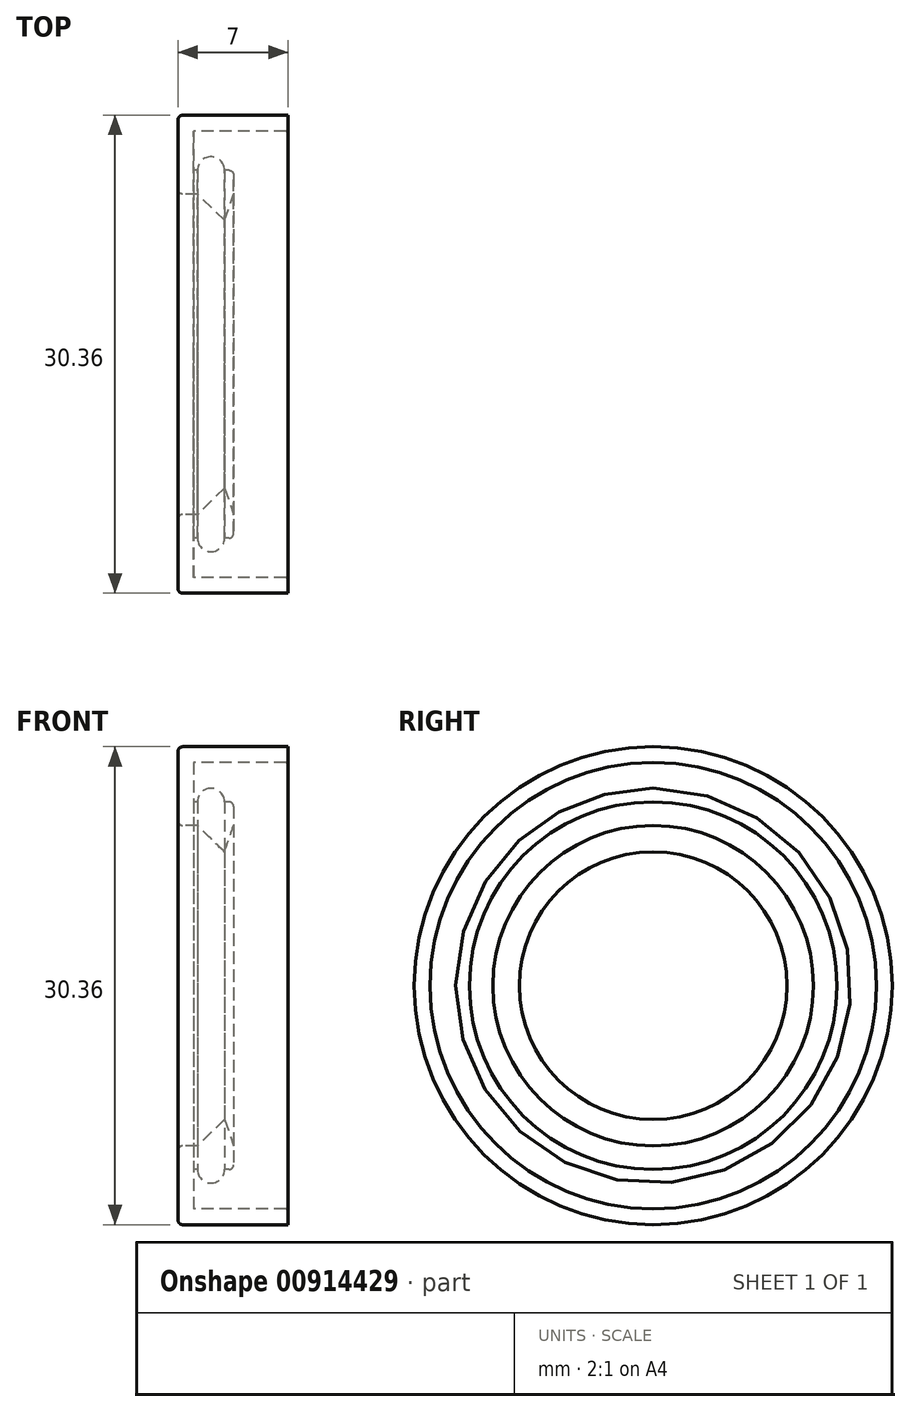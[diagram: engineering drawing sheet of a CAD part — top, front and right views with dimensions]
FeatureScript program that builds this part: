
annotation { "Feature Type Name" : "Feature", "Feature Type Description" : "" }
export const myFeature = defineFeature(function(context is Context, id is Id, definition is map)
    precondition{}
    {
        {
            var Q0;
            Q0=qCreatedBy(makeId("Front.planeOp"),FACE);
            var sketch = newSketch(context, id + "F0", { "sketchPlane" : qUnion([Q0])});
            skLineSegment(sketch, "E0", {"start": v(0, 15.18) * mm, "end": v(0, 0) * mm, "construction": true});
            skLineSegment(sketch, "E1", {"start": v(0, 0) * mm, "end": v(16, 0) * mm, "construction": true});
            skLineSegment(sketch, "E2", {"start": v(3.47, 15.18) * mm, "end": v(-3.23, 15.18) * mm});
            skLineSegment(sketch, "E3", {"start": v(-3.53, 14.88) * mm, "end": v(-3.53, 10.48) * mm});
            skLineSegment(sketch, "E4", {"start": v(-3.23, 10.18) * mm, "end": v(-2.3, 10.18) * mm});
            skLineSegment(sketch, "E5", {"start": v(-2.3, 10.18) * mm, "end": v(-0.58, 8.5) * mm});
            skLineSegment(sketch, "E6", {"start": v(-0.58, 8.5) * mm, "end": v(0, 10.18) * mm});
            skLineSegment(sketch, "E7", {"start": v(0, 10.18) * mm, "end": v(0, 11.38) * mm});
            skLineSegment(sketch, "E8", {"start": v(-0.3, 11.68) * mm, "end": v(-0.58, 11.68) * mm});
            skArc(sketch, "E9", {"start": v(-0.58, 11.68) * mm, "mid": v(-1.44, 12.54) * mm, "end": v(-2.3, 11.68) * mm});
            skLineSegment(sketch, "E10", {"start": v(-2.3, 11.68) * mm, "end": v(-2.53, 11.68) * mm});
            skLineSegment(sketch, "E11", {"start": v(-2.53, 11.68) * mm, "end": v(-2.53, 14.18) * mm});
            skLineSegment(sketch, "E12", {"start": v(-2.53, 14.18) * mm, "end": v(3.32, 14.18) * mm});
            skLineSegment(sketch, "E13", {"start": v(3.47, 14.32) * mm, "end": v(3.47, 15.18) * mm});
            skPoint(sketch, "E14.visualSharp", {"position": v(3.47, 14.18) * mm});
            skArc(sketch, "E14.filletArc", {"start": v(3.32, 14.18) * mm, "mid": v(3.43, 14.22) * mm, "end": v(3.47, 14.32) * mm});
            skPoint(sketch, "E15.visualSharp", {"position": v(-3.53, 15.18) * mm});
            skArc(sketch, "E15.filletArc", {"start": v(-3.23, 15.18) * mm, "mid": v(-3.44, 15.1) * mm, "end": v(-3.53, 14.88) * mm});
            skPoint(sketch, "E16.visualSharp", {"position": v(0, 11.68) * mm});
            skArc(sketch, "E16.filletArc", {"start": v(0, 11.38) * mm, "mid": v(-0.09, 11.6) * mm, "end": v(-0.3, 11.68) * mm});
            skPoint(sketch, "E17.visualSharp", {"position": v(-3.53, 10.18) * mm});
            skArc(sketch, "E17.filletArc", {"start": v(-3.53, 10.48) * mm, "mid": v(-3.44, 10.27) * mm, "end": v(-3.23, 10.18) * mm});
            skSolve(sketch);
        }
        {
            var Q0;
            Q0 = qSketchRegion(id + "F0", true);
            var Q1;
            Q1=sQuery(id+"F0.wireOp",EDGE,"E1");
            revolve(context, id + "F1", {"surfaceOperationType" : NewSurfaceOperationType.NEW, "entities" : qUnion([Q0]), "axis" : qUnion([Q1]), "revolveType" : RevolveType.FULL});
        }
    });
